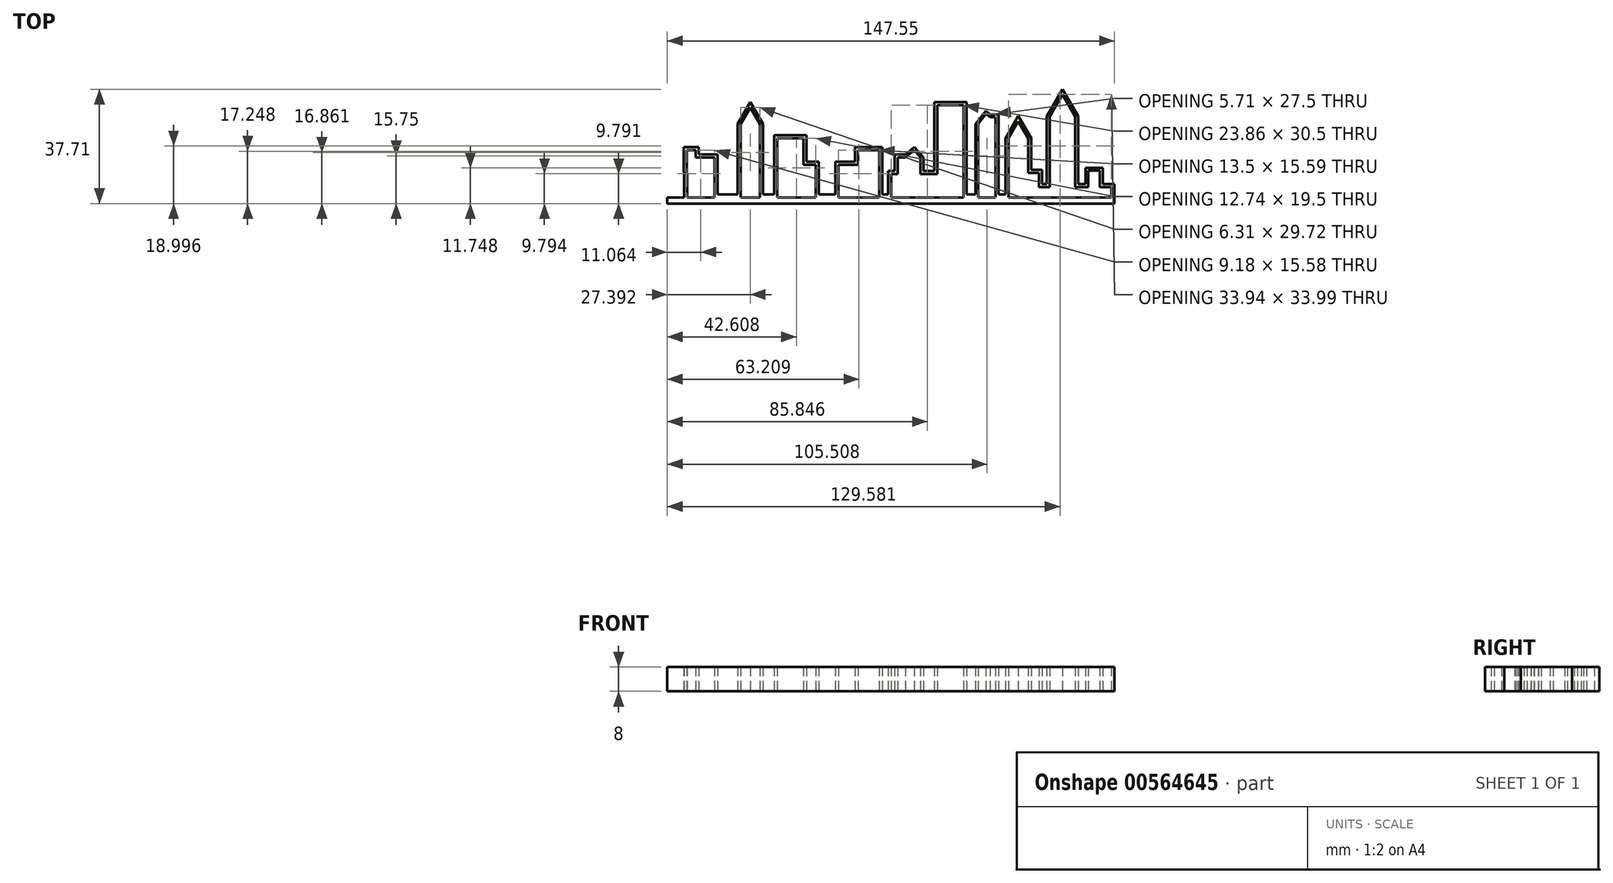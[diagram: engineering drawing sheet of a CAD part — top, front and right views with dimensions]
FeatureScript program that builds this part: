
annotation { "Feature Type Name" : "Feature", "Feature Type Description" : "" }
export const myFeature = defineFeature(function(context is Context, id is Id, definition is map)
    precondition{}
    {
        {
            var Q0;
            Q0=qCreatedBy(makeId("Top.planeOp"),FACE);
            var sketch = newSketch(context, id + "F0", { "sketchPlane" : qUnion([Q0])});
            skLineSegment(sketch, "E0", {"start": v(-8.8, 15.59) * mm, "end": v(-8.8, 10.82) * mm});
            skLineSegment(sketch, "E1", {"start": v(-8.8, 10.82) * mm, "end": v(-15.3, 10.82) * mm});
            skLineSegment(sketch, "E2", {"start": v(-15.3, 10.82) * mm, "end": v(-15.3, 1) * mm});
            skLineSegment(sketch, "E3", {"start": v(-17.9, 0) * mm, "end": v(-22.77, 0) * mm});
            skLineSegment(sketch, "E4", {"start": v(-22.77, 0) * mm, "end": v(-22.77, 10.82) * mm});
            skLineSegment(sketch, "E5", {"start": v(-26.82, 10.82) * mm, "end": v(-22.77, 10.82) * mm});
            skLineSegment(sketch, "E6", {"start": v(-26.82, 10.82) * mm, "end": v(-26.82, 19.5) * mm});
            skLineSegment(sketch, "E7", {"start": v(-26.82, 19.5) * mm, "end": v(-35.51, 19.5) * mm});
            skLineSegment(sketch, "E8", {"start": v(-35.51, 19.5) * mm, "end": v(-35.51, 0) * mm});
            skLineSegment(sketch, "E9", {"start": v(-35.51, 0) * mm, "end": v(-41.2, 0) * mm});
            skLineSegment(sketch, "E10", {"start": v(-41.2, 0) * mm, "end": v(-41.2, 24.26) * mm});
            skLineSegment(sketch, "E11", {"start": v(-41.2, 24.26) * mm, "end": v(-44.36, 29.72) * mm});
            skLineSegment(sketch, "E12", {"start": v(-47.51, 0) * mm, "end": v(-51.85, 0) * mm});
            skLineSegment(sketch, "E13", {"start": v(0, 0) * mm, "end": v(2.17, 0) * mm});
            skLineSegment(sketch, "E14", {"start": v(2.17, 0) * mm, "end": v(2.17, 7.73) * mm});
            skLineSegment(sketch, "E15", {"start": v(2.17, 7.73) * mm, "end": v(4.34, 7.73) * mm});
            skLineSegment(sketch, "E16", {"start": v(4.34, 7.73) * mm, "end": v(4.34, 13.15) * mm});
            skLineSegment(sketch, "E17", {"start": v(4.34, 13.15) * mm, "end": v(6.78, 13.15) * mm});
            skLineSegment(sketch, "E18", {"start": v(6.78, 13.15) * mm, "end": v(9.76, 15.59) * mm});
            skLineSegment(sketch, "E19", {"start": v(9.76, 15.59) * mm, "end": v(11.76, 13.15) * mm});
            skLineSegment(sketch, "E20", {"start": v(11.76, 13.15) * mm, "end": v(11.76, 7.73) * mm});
            skLineSegment(sketch, "E21", {"start": v(11.76, 7.73) * mm, "end": v(17.35, 7.73) * mm});
            skLineSegment(sketch, "E22", {"start": v(17.35, 7.73) * mm, "end": v(17.35, 30.5) * mm});
            skLineSegment(sketch, "E23", {"start": v(17.35, 30.5) * mm, "end": v(26.02, 30.5) * mm});
            skLineSegment(sketch, "E24", {"start": v(26.02, 30.5) * mm, "end": v(26.02, 7.73) * mm});
            skLineSegment(sketch, "E25", {"start": v(26.02, 7.73) * mm, "end": v(26.02, 0) * mm});
            skLineSegment(sketch, "E26", {"start": v(26.02, 0) * mm, "end": v(30.9, 0) * mm});
            skLineSegment(sketch, "E27", {"start": v(30.9, 0) * mm, "end": v(30.9, 19.5) * mm});
            skLineSegment(sketch, "E28", {"start": v(30.9, 19.5) * mm, "end": v(30.9, 24.26) * mm});
            skLineSegment(sketch, "E29", {"start": v(30.9, 24.26) * mm, "end": v(33.42, 27.5) * mm});
            skLineSegment(sketch, "E30", {"start": v(33.42, 27.5) * mm, "end": v(34.76, 26.45) * mm});
            skLineSegment(sketch, "E31", {"start": v(34.76, 26.45) * mm, "end": v(36.61, 26.45) * mm});
            skLineSegment(sketch, "E32", {"start": v(36.61, 26.45) * mm, "end": v(36.61, 24.26) * mm});
            skLineSegment(sketch, "E33", {"start": v(36.61, 24.26) * mm, "end": v(36.61, 0) * mm});
            skLineSegment(sketch, "E34", {"start": v(44.1, 25.12) * mm, "end": v(47.36, 19.5) * mm});
            skLineSegment(sketch, "E35", {"start": v(47.36, 19.5) * mm, "end": v(47.36, 8.1) * mm});
            skLineSegment(sketch, "E36", {"start": v(47.36, 8.1) * mm, "end": v(50.96, 8.1) * mm});
            skLineSegment(sketch, "E37", {"start": v(50.96, 8.1) * mm, "end": v(50.96, 3.39) * mm});
            skLineSegment(sketch, "E38", {"start": v(50.96, 3.39) * mm, "end": v(54.48, 3.39) * mm});
            skLineSegment(sketch, "E39", {"start": v(58.69, 34) * mm, "end": v(62.89, 26.71) * mm});
            skLineSegment(sketch, "E40", {"start": v(67.21, 3.39) * mm, "end": v(67.21, 8.81) * mm});
            skLineSegment(sketch, "E41", {"start": v(67.21, 8.81) * mm, "end": v(71, 8.81) * mm});
            skPoint(sketch, "E42.start.orphan", {"position": v(-66.14, 14.37) * mm});
            skLineSegment(sketch, "E43", {"start": v(-71.73, -2) * mm, "end": v(74.8, -2) * mm});
            skLineSegment(sketch, "E44", {"start": v(-66.14, 0) * mm, "end": v(74.8, 0) * mm});
            skLineSegment(sketch, "E45", {"start": v(74.8, 3.39) * mm, "end": v(74.8, 0) * mm});
            skPoint(sketch, "E46.orphan", {"position": v(76.22, -2) * mm});
            skLineSegment(sketch, "E47", {"start": v(74.8, -2) * mm, "end": v(75.8, -2) * mm});
            skLineSegment(sketch, "E48", {"start": v(75.8, -2) * mm, "end": v(75.8, 4.39) * mm});
            skPoint(sketch, "E49.start.orphan", {"position": v(72.9, 3.39) * mm});
            skLineSegment(sketch, "E50", {"start": v(74.8, 4.39) * mm, "end": v(72, 4.39) * mm});
            skLineSegment(sketch, "E51", {"start": v(72, 4.39) * mm, "end": v(72, 9.81) * mm});
            skLineSegment(sketch, "E52", {"start": v(68.57, 9.81) * mm, "end": v(72, 9.81) * mm});
            skLineSegment(sketch, "E53", {"start": v(74.8, 0) * mm, "end": v(75.8, 0) * mm});
            skLineSegment(sketch, "E54", {"start": v(66.21, 6.69) * mm, "end": v(66.21, 9.81) * mm});
            skLineSegment(sketch, "E55", {"start": v(68.57, 9.81) * mm, "end": v(66.21, 9.81) * mm});
            skLineSegment(sketch, "E56", {"start": v(66.21, 6.69) * mm, "end": v(66.21, 4.39) * mm});
            skLineSegment(sketch, "E57", {"start": v(64.7, 4.39) * mm, "end": v(66.21, 4.39) * mm});
            skLineSegment(sketch, "E58", {"start": v(64.7, 4.39) * mm, "end": v(63.88, 4.39) * mm});
            skLineSegment(sketch, "E59", {"start": v(54.48, 3.39) * mm, "end": v(54.48, 26.71) * mm});
            skLineSegment(sketch, "E60", {"start": v(53.48, 26.68) * mm, "end": v(53.48, 4.39) * mm});
            skLineSegment(sketch, "E61", {"start": v(53.48, 4.39) * mm, "end": v(51.96, 4.39) * mm});
            skLineSegment(sketch, "E62", {"start": v(51.96, 4.39) * mm, "end": v(51.96, 9.1) * mm});
            skLineSegment(sketch, "E63", {"start": v(51.96, 9.1) * mm, "end": v(48.36, 9.1) * mm});
            skPoint(sketch, "E64.start.orphan", {"position": v(39.32, 19.5) * mm});
            skLineSegment(sketch, "E65", {"start": v(54.48, 3.39) * mm, "end": v(74.8, 3.39) * mm});
            skLineSegment(sketch, "E66", {"start": v(71, 8.81) * mm, "end": v(71, 3.39) * mm});
            skPoint(sketch, "E67.orphan", {"position": v(71, 3.39) * mm});
            skPoint(sketch, "E68.orphan", {"position": v(74.8, 3.39) * mm});
            skPoint(sketch, "E69.end.orphan", {"position": v(62.88, 3.39) * mm});
            skLineSegment(sketch, "E70", {"start": v(62.89, 26.71) * mm, "end": v(62.89, 3.39) * mm});
            skLineSegment(sketch, "E71", {"start": v(62.89, 26.71) * mm, "end": v(54.48, 26.71) * mm});
            skLineSegment(sketch, "E72", {"start": v(54.48, 26.71) * mm, "end": v(58.69, 34) * mm});
            skLineSegment(sketch, "E73", {"start": v(63.89, 26.71) * mm, "end": v(63.88, 4.39) * mm});
            skLineSegment(sketch, "E74", {"start": v(63.89, 26.71) * mm, "end": v(58.7, 35.7) * mm});
            skLineSegment(sketch, "E75", {"start": v(53.48, 26.68) * mm, "end": v(58.7, 35.7) * mm});
            skLineSegment(sketch, "E76", {"start": v(48.36, 19.5) * mm, "end": v(48.36, 9.1) * mm});
            skLineSegment(sketch, "E77", {"start": v(48.36, 19.5) * mm, "end": v(44.1, 26.86) * mm});
            skLineSegment(sketch, "E78", {"start": v(37.61, 1) * mm, "end": v(37.61, 27.45) * mm});
            skLineSegment(sketch, "E79", {"start": v(34.76, 27.45) * mm, "end": v(37.61, 27.45) * mm});
            skLineSegment(sketch, "E80", {"start": v(34.23, 27.87) * mm, "end": v(34.41, 28.1) * mm});
            skLineSegment(sketch, "E81", {"start": v(34.76, 27.45) * mm, "end": v(33.42, 28.5) * mm});
            skLineSegment(sketch, "E82", {"start": v(33.42, 28.5) * mm, "end": v(29.9, 24.26) * mm});
            skLineSegment(sketch, "E83", {"start": v(29.9, 24.26) * mm, "end": v(29.9, 1) * mm});
            skPoint(sketch, "E84.start.orphan", {"position": v(28.46, 0) * mm});
            skLineSegment(sketch, "E85", {"start": v(29.9, 1) * mm, "end": v(27.02, 1) * mm});
            skLineSegment(sketch, "E86", {"start": v(27.02, 1) * mm, "end": v(27.02, 31.5) * mm});
            skPoint(sketch, "E87.start.orphan", {"position": v(21.69, 30.5) * mm});
            skLineSegment(sketch, "E88", {"start": v(27.02, 31.5) * mm, "end": v(16.35, 31.5) * mm});
            skLineSegment(sketch, "E89", {"start": v(16.35, 31.5) * mm, "end": v(16.35, 8.73) * mm});
            skPoint(sketch, "E90.start.orphan", {"position": v(14.55, 7.73) * mm});
            skLineSegment(sketch, "E91", {"start": v(16.35, 8.73) * mm, "end": v(12.76, 8.73) * mm});
            skLineSegment(sketch, "E92", {"start": v(12.76, 8.73) * mm, "end": v(12.76, 13.15) * mm});
            skLineSegment(sketch, "E93", {"start": v(4.34, 14.15) * mm, "end": v(6.78, 14.15) * mm});
            skLineSegment(sketch, "E94", {"start": v(6.78, 14.15) * mm, "end": v(9.76, 16.59) * mm});
            skLineSegment(sketch, "E95", {"start": v(12.76, 13.15) * mm, "end": v(9.76, 16.59) * mm});
            skLineSegment(sketch, "E96", {"start": v(4.34, 14.15) * mm, "end": v(3.34, 14.15) * mm});
            skLineSegment(sketch, "E97", {"start": v(3.34, 14.15) * mm, "end": v(3.34, 8.73) * mm});
            skLineSegment(sketch, "E98", {"start": v(-8.8, 15.59) * mm, "end": v(-1.8, 15.59) * mm});
            skLineSegment(sketch, "E99", {"start": v(-1.8, 15.59) * mm, "end": v(-1.8, 0) * mm});
            skLineSegment(sketch, "E100", {"start": v(3.34, 8.73) * mm, "end": v(1.17, 8.73) * mm});
            skLineSegment(sketch, "E101", {"start": v(1.17, 8.73) * mm, "end": v(1.17, 1) * mm});
            skLineSegment(sketch, "E102", {"start": v(1.17, 1) * mm, "end": v(-0.8, 1) * mm});
            skLineSegment(sketch, "E103", {"start": v(-0.8, 1) * mm, "end": v(-0.8, 16.59) * mm});
            skLineSegment(sketch, "E104", {"start": v(-0.8, 16.59) * mm, "end": v(-9.8, 16.59) * mm});
            skLineSegment(sketch, "E105", {"start": v(-9.8, 16.59) * mm, "end": v(-9.8, 11.82) * mm});
            skLineSegment(sketch, "E106", {"start": v(-9.8, 11.82) * mm, "end": v(-16.3, 11.82) * mm});
            skPoint(sketch, "E107.start.orphan", {"position": v(-20.33, 0) * mm});
            skLineSegment(sketch, "E108", {"start": v(-21.77, 1) * mm, "end": v(-21.77, 11.82) * mm});
            skLineSegment(sketch, "E109", {"start": v(-21.77, 11.82) * mm, "end": v(-25.82, 11.82) * mm});
            skLineSegment(sketch, "E110", {"start": v(-25.82, 11.82) * mm, "end": v(-25.82, 20.5) * mm});
            skLineSegment(sketch, "E111", {"start": v(-30.47, 20.5) * mm, "end": v(-25.82, 20.5) * mm});
            skLineSegment(sketch, "E112", {"start": v(-30.47, 20.5) * mm, "end": v(-36.51, 20.5) * mm});
            skPoint(sketch, "E113.start.orphan", {"position": v(-26.82, 15.16) * mm});
            skLineSegment(sketch, "E114", {"start": v(-36.51, 20.5) * mm, "end": v(-36.51, 1) * mm});
            skLineSegment(sketch, "E115", {"start": v(-36.51, 1) * mm, "end": v(-40.2, 1) * mm});
            skLineSegment(sketch, "E116", {"start": v(-40.2, 1) * mm, "end": v(-40.2, 24.26) * mm});
            skLineSegment(sketch, "E117", {"start": v(-41.2, 24.26) * mm, "end": v(-47.51, 24.26) * mm});
            skPoint(sketch, "E118.start.orphan", {"position": v(-47.51, 24.26) * mm});
            skPoint(sketch, "E119.end.orphan", {"position": v(-50.96, 1) * mm});
            skLineSegment(sketch, "E120", {"start": v(-47.51, 0) * mm, "end": v(-47.51, 24.26) * mm});
            skLineSegment(sketch, "E121", {"start": v(-47.51, 24.26) * mm, "end": v(-44.36, 29.72) * mm});
            skLineSegment(sketch, "E122", {"start": v(-48.51, 24.26) * mm, "end": v(-44.36, 31.45) * mm});
            skLineSegment(sketch, "E123", {"start": v(-40.2, 24.26) * mm, "end": v(-44.36, 31.45) * mm});
            skLineSegment(sketch, "E124", {"start": v(-48.51, 24.26) * mm, "end": v(-48.51, 1) * mm});
            skPoint(sketch, "E125.end.orphan", {"position": v(-55.1, 0) * mm});
            skPoint(sketch, "E126.orphan", {"position": v(-55.1, 1) * mm});
            skLineSegment(sketch, "E127", {"start": v(-16.3, 11.82) * mm, "end": v(-16.3, 1) * mm});
            skLineSegment(sketch, "E128", {"start": v(-21.77, 1) * mm, "end": v(-16.3, 1) * mm});
            skLineSegment(sketch, "E129", {"start": v(-15.3, 1) * mm, "end": v(-15.3, 0) * mm});
            skLineSegment(sketch, "E130", {"start": v(74.8, 4.39) * mm, "end": v(75.8, 4.39) * mm});
            skLineSegment(sketch, "E131", {"start": v(47.36, 19.5) * mm, "end": v(40.86, 19.5) * mm});
            skLineSegment(sketch, "E132", {"start": v(40.86, 19.5) * mm, "end": v(44.1, 25.12) * mm});
            skPoint(sketch, "E133.orphan", {"position": v(43.34, 26.45) * mm});
            skLineSegment(sketch, "E134", {"start": v(39.86, 19.5) * mm, "end": v(44.1, 26.86) * mm});
            skLineSegment(sketch, "E135", {"start": v(39.86, 19.5) * mm, "end": v(39.86, 1) * mm});
            skLineSegment(sketch, "E136", {"start": v(40.86, 19.5) * mm, "end": v(40.86, 0) * mm});
            skLineSegment(sketch, "E137", {"start": v(37.61, 1) * mm, "end": v(39.86, 1) * mm});
            skLineSegment(sketch, "E138", {"start": v(-48.51, 1) * mm, "end": v(-55.1, 1) * mm});
            skLineSegment(sketch, "E139", {"start": v(-55.1, 1) * mm, "end": v(-55.1, 14.2) * mm});
            skLineSegment(sketch, "E140", {"start": v(-55.1, 14.2) * mm, "end": v(-61.35, 14.2) * mm});
            skLineSegment(sketch, "E141", {"start": v(-61.35, 14.2) * mm, "end": v(-61.35, 16.56) * mm});
            skLineSegment(sketch, "E142", {"start": v(-61.35, 16.56) * mm, "end": v(-66.28, 16.56) * mm});
            skPoint(sketch, "E143.end.orphan", {"position": v(-66.14, 15.59) * mm});
            skPoint(sketch, "E144.end.orphan", {"position": v(-66.14, 13.15) * mm});
            skLineSegment(sketch, "E145", {"start": v(-66.28, 16.56) * mm, "end": v(-66.14, 0) * mm});
            skLineSegment(sketch, "E146", {"start": v(-66.14, 0) * mm, "end": v(-71.75, -0.05) * mm});
            skLineSegment(sketch, "E147", {"start": v(-71.75, -0.05) * mm, "end": v(-71.73, -2) * mm});
            skPoint(sketch, "E148.start.orphan", {"position": v(-63.82, 16.56) * mm});
            skLineSegment(sketch, "E149", {"start": v(-65.28, 15.56) * mm, "end": v(-62.35, 15.58) * mm});
            skLineSegment(sketch, "E150", {"start": v(-62.35, 15.06) * mm, "end": v(-62.35, 15.58) * mm});
            skLineSegment(sketch, "E151", {"start": v(-62.35, 15.06) * mm, "end": v(-62.35, 13.2) * mm});
            skLineSegment(sketch, "E152", {"start": v(-62.35, 13.2) * mm, "end": v(-56.1, 13.2) * mm});
            skLineSegment(sketch, "E153", {"start": v(-65.28, 15.56) * mm, "end": v(-65.14, 0) * mm});
            skLineSegment(sketch, "E154", {"start": v(-56.1, 13.2) * mm, "end": v(-56.1, 0) * mm});
            skSolve(sketch);
        }
        {
            var Q0;
            Q0 = qSketchRegion(id + "F0", true);
            extrude(context, id + "F1", {"entities" : qUnion([Q0]), "depth" : 8 * mm, "offsetDistance" : 25 * mm});
        }
    });
